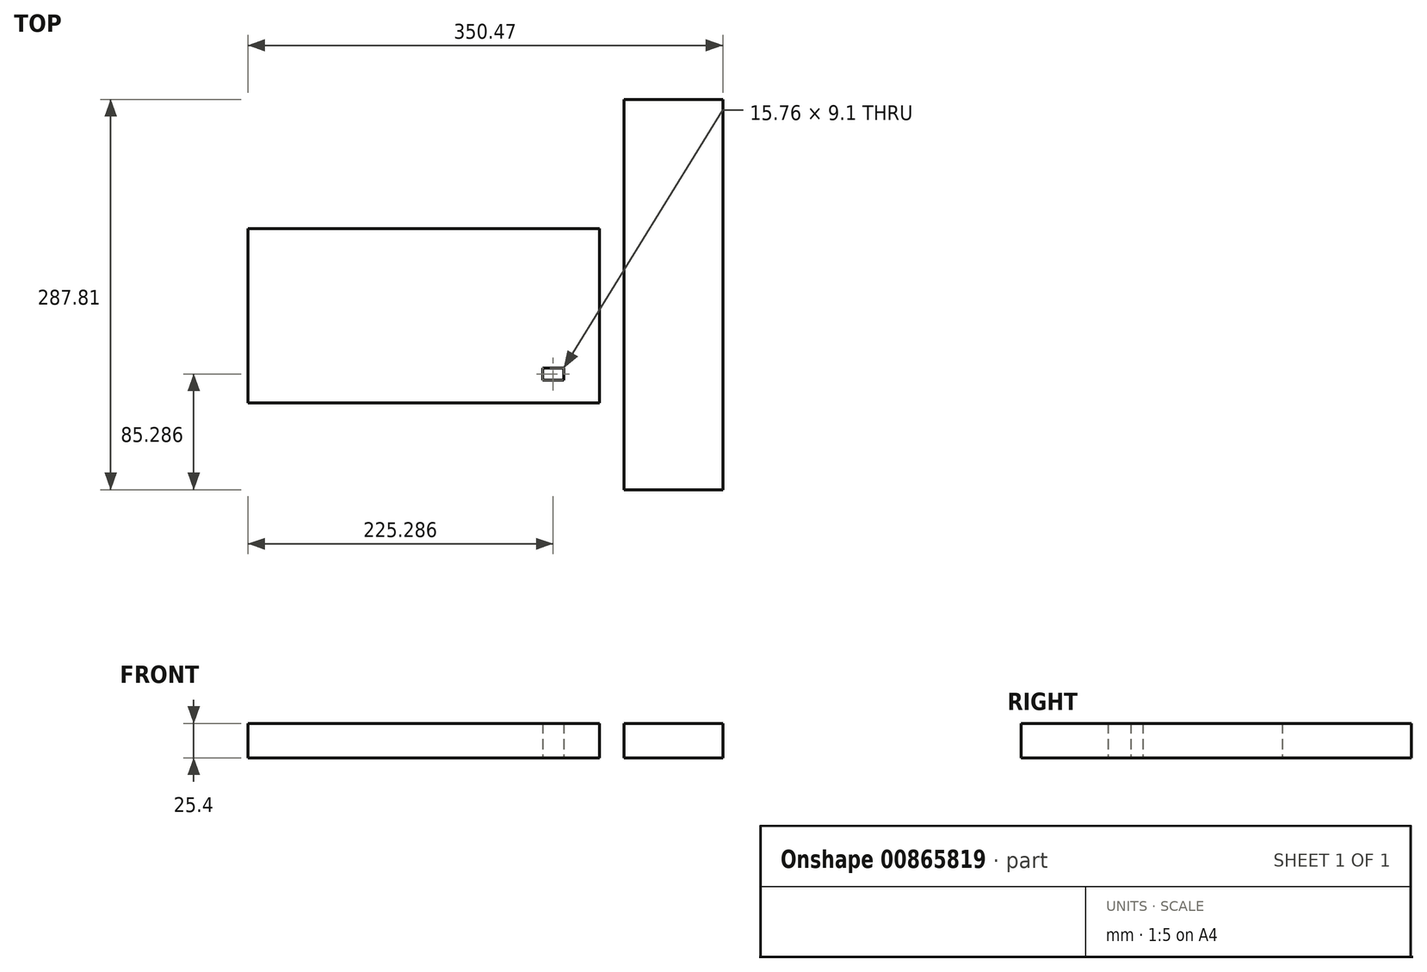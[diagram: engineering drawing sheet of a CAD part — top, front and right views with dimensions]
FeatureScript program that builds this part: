
annotation { "Feature Type Name" : "Feature", "Feature Type Description" : "" }
export const myFeature = defineFeature(function(context is Context, id is Id, definition is map)
    precondition{}
    {
        {
            var Q0;
            Q0=qCreatedBy(makeId("Top.planeOp"),FACE);
            var sketch = newSketch(context, id + "F0", { "sketchPlane" : qUnion([Q0])});
            skLineSegment(sketch, "E0.bottom", {"start": v(0, 0) * mm, "end": v(-259.37, 0) * mm});
            skLineSegment(sketch, "E0.top", {"start": v(0, 128.6) * mm, "end": v(-259.37, 128.6) * mm});
            skLineSegment(sketch, "E0.left", {"start": v(0, 0) * mm, "end": v(0, 128.6) * mm});
            skLineSegment(sketch, "E0.right", {"start": v(-259.37, 0) * mm, "end": v(-259.37, 128.6) * mm});
            skLineSegment(sketch, "E1.bottom", {"start": v(-26.2, 25.83) * mm, "end": v(-41.96, 25.83) * mm});
            skLineSegment(sketch, "E1.top", {"start": v(-26.2, 16.74) * mm, "end": v(-41.96, 16.74) * mm});
            skLineSegment(sketch, "E1.left", {"start": v(-26.2, 25.83) * mm, "end": v(-26.2, 16.74) * mm});
            skLineSegment(sketch, "E1.right", {"start": v(-41.96, 25.83) * mm, "end": v(-41.96, 16.74) * mm});
            skLineSegment(sketch, "E2.bottom", {"start": v(18.3, -64) * mm, "end": v(91.1, -64) * mm});
            skLineSegment(sketch, "E2.top", {"start": v(18.3, 223.8) * mm, "end": v(91.1, 223.8) * mm});
            skLineSegment(sketch, "E2.left", {"start": v(18.3, -64) * mm, "end": v(18.3, 223.8) * mm});
            skLineSegment(sketch, "E2.right", {"start": v(91.1, -64) * mm, "end": v(91.1, 223.8) * mm});
            skSolve(sketch);
        }
        {
            var Q0;
            Q0 = qSketchRegion(id + "F0", true);
            var Q1;
            Q1=makeQuery(id+"F0.imprint","IMPRINT",FACE,{"disambiguationData":[TD([[makeQuery(id+"F0.imprint","IMPRINT",EDGE,{"derivedFrom":sQuery(id+"F0.wireOp",EDGE,"E0.bottom")}),-1.0]])]});
            extrude(context, id + "F1", {"entities" : qUnion([Q0, Q1]), "depth" : 25.4 * mm, "offsetDistance" : 25.4 * mm});
        }
    });
